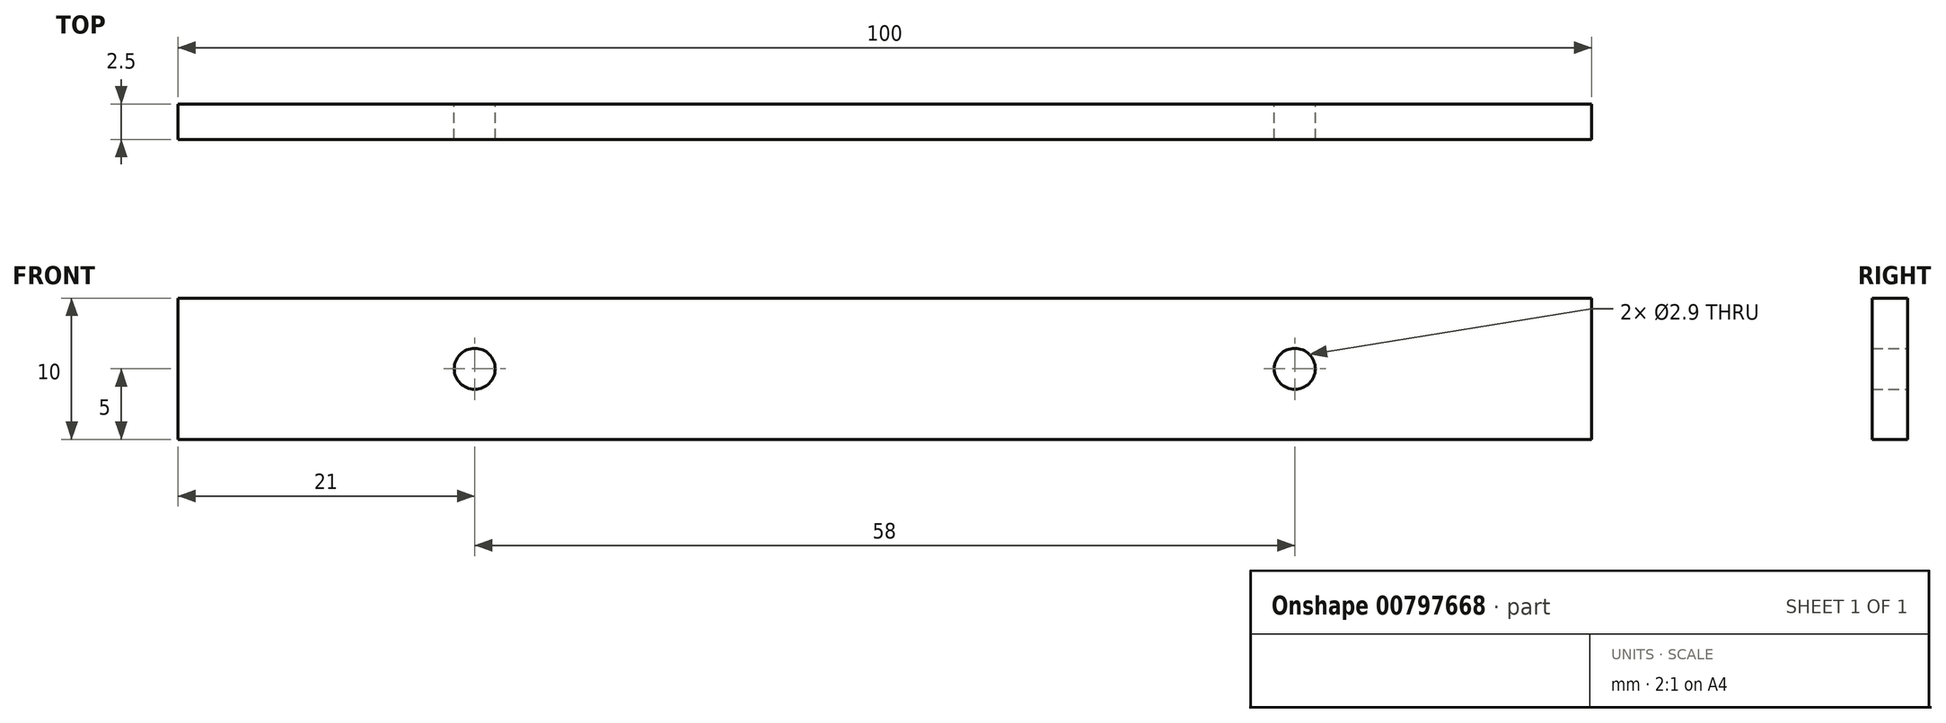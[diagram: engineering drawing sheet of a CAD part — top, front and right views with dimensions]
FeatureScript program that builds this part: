
annotation { "Feature Type Name" : "Feature", "Feature Type Description" : "" }
export const myFeature = defineFeature(function(context is Context, id is Id, definition is map)
    precondition{}
    {
        {
            var Q0;
            Q0=qCreatedBy(makeId("Front.planeOp"),FACE);
            var sketch = newSketch(context, id + "F0", { "sketchPlane" : qUnion([Q0])});
            skLineSegment(sketch, "E0.bottom", {"start": v(-50, 5) * mm, "end": v(50, 5) * mm});
            skLineSegment(sketch, "E0.top", {"start": v(-50, -5) * mm, "end": v(50, -5) * mm});
            skLineSegment(sketch, "E0.left", {"start": v(-50, 5) * mm, "end": v(-50, -5) * mm});
            skLineSegment(sketch, "E0.right", {"start": v(50, 5) * mm, "end": v(50, -5) * mm});
            skCircle(sketch, "E1", {"center": v(-29, 0) * mm, "radius": 1.45 * mm});
            skCircle(sketch, "E2.MirrorC", {"center": v(29, 0) * mm, "radius": 1.45 * mm});
            skSolve(sketch);
        }
        {
            var Q0;
            Q0=qSketchRegion(id+"F0",true);
            extrude(context, id + "F1", {"entities" : qUnion([Q0]), "depth" : 2.5 * mm, "offsetDistance" : 25 * mm});
        }
    });
